# Revit family: Hand_Shower-GROHE-Euphoria_110_26513000
name_source: partatom
category: Plumbing Fixtures
revit_build: Autodesk Revit 2014 (Build: 20130308_1515(x64)
units: mm (PartAtom-declared; Revit-internal decimal feet)

## types (1)
- 26513000
    Assembly Code = D2010710
    CW Connection = Yes
    CWFU = 3
    Cold Water Connection Diameter = 1/2"
    Cold Water Connection Radius = 1/4"
    Default Elevation = 0"
    Description = Euphoria 110 Massage Handshower 3 sprays
    Finish = Metal-Grohe-000-Chrome
    Flow Rate = 1.75 gpm (6.6 L/min)
    HW Connection = Yes
    HWFU = 3
    Height = 7 7/16"
    Hot Water Connection Diameter = 1"
    Hot Water Connection Radius = 1/4"
    Manufacturer = Grohe
    Material = Metal-Grohe-000-Chrome
    Model = 26513000
    Price = Prices may vary. Please consult Manufacturer Representative for most up-to-date price list.
    Product Page URL = https://www.grohe.us
    Tempered Connection Diameter = 1/2"
    Tempered Connection Radius = 1/4"
    URL = https://www.grohe.us
    Vent Connection = No
    WFU = 4
    Warranty Documentation Link = https://cdn.cloud.grohe.com
    Waste Connection = No
    cUPC Compliant = Yes

## geometry (parser evidence)
native form markers: Sweep x1
no freeform markers — native parametric forms only
